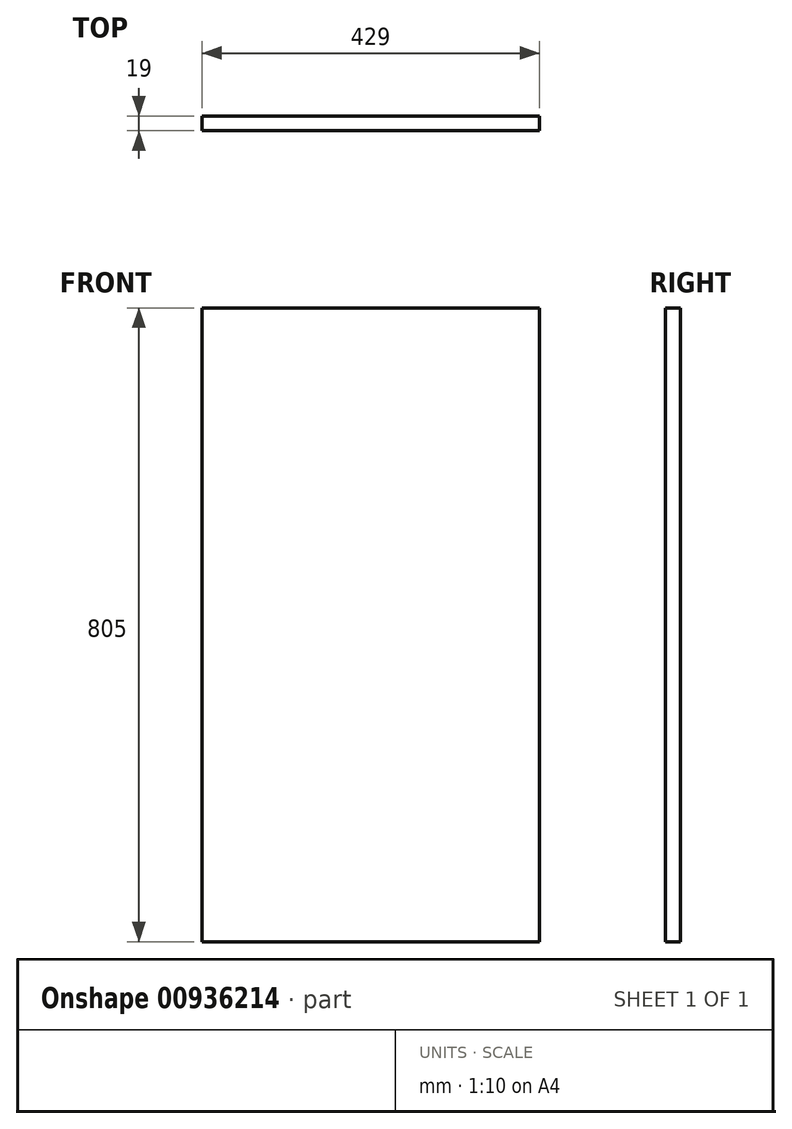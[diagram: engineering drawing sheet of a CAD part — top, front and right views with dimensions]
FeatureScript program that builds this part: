
annotation { "Feature Type Name" : "Feature", "Feature Type Description" : "" }
export const myFeature = defineFeature(function(context is Context, id is Id, definition is map)
    precondition{}
    {
        {
            var Q0;
            Q0=qCreatedBy(makeId("Front.planeOp"),FACE);
            var sketch = newSketch(context, id + "F0", { "sketchPlane" : qUnion([Q0])});
            skLineSegment(sketch, "E0.bottom", {"start": v(0, 0) * mm, "end": v(429, 0) * mm});
            skLineSegment(sketch, "E0.top", {"start": v(0, 805) * mm, "end": v(429, 805) * mm});
            skLineSegment(sketch, "E0.left", {"start": v(0, 0) * mm, "end": v(0, 805) * mm});
            skLineSegment(sketch, "E0.right", {"start": v(429, 0) * mm, "end": v(429, 805) * mm});
            skSolve(sketch);
        }
        {
            var Q0;
            Q0=makeQuery(id+"F0.imprint","IMPRINT",FACE,{"disambiguationData":[TD([[makeQuery(id+"F0.imprint","IMPRINT",EDGE,{"derivedFrom":sQuery(id+"F0.wireOp",EDGE,"E0.bottom")}),1.0]])]});
            extrude(context, id + "F1", {"entities" : qUnion([Q0]), "depth" : 19 * mm, "offsetDistance" : 25 * mm});
        }
    });
